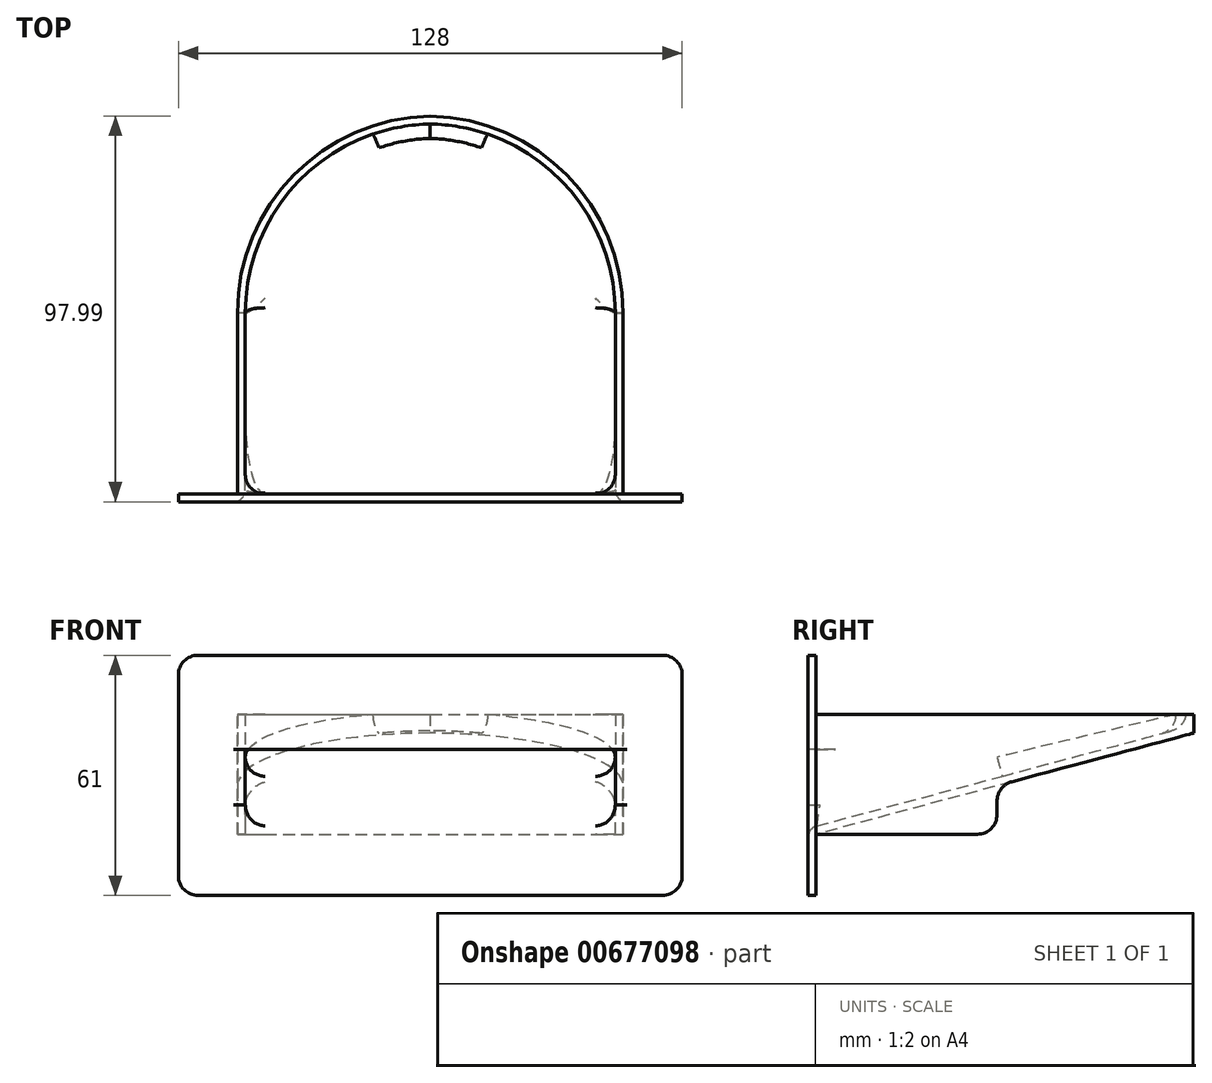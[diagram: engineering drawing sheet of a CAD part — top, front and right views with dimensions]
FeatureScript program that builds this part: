
annotation { "Feature Type Name" : "Feature", "Feature Type Description" : "" }
export const myFeature = defineFeature(function(context is Context, id is Id, definition is map)
    precondition{}
    {
        {
            var Q0;
            Q0=qCreatedBy(makeId("Front.planeOp"),FACE);
            var sketch = newSketch(context, id + "F0", { "sketchPlane" : qUnion([Q0])});
            skLineSegment(sketch, "E0.bottom", {"start": v(0, 0) * mm, "end": v(98, 0) * mm});
            skLineSegment(sketch, "E0.top", {"start": v(0, 31) * mm, "end": v(98, 31) * mm});
            skLineSegment(sketch, "E0.left", {"start": v(0, 0) * mm, "end": v(0, 31) * mm});
            skLineSegment(sketch, "E0.right", {"start": v(98, 0) * mm, "end": v(98, 31) * mm});
            skSolve(sketch);
        }
        {
            var Q0;
            Q0=makeQuery(id+"F0.imprint","IMPRINT",FACE,{"disambiguationData":[TD([[makeQuery(id+"F0.imprint","IMPRINT",EDGE,{"derivedFrom":sQuery(id+"F0.wireOp",EDGE,"E0.bottom")}),1.0]])]});
            extrude(context, id + "F1", {"entities" : qUnion([Q0]), "oppositeDirection" : true, "depth" : 98 * mm, "offsetDistance" : 25 * mm});
        }
        {
            var Q0;
            Q0=makeQuery(id+"F1.opExtrude","CAP_EDGE",EDGE,{"disambiguationData":[OSD([sQuery(id+"F0.wireOp",EDGE,"E0.right")])],"isStart":false});
            var Q1;
            Q1=makeQuery(id+"F1.opExtrude","CAP_EDGE",EDGE,{"disambiguationData":[OSD([sQuery(id+"F0.wireOp",EDGE,"E0.left")])],"isStart":false});
            fillet(context, id + "F2", {"entities" : qUnion([Q0, Q1]), "radius" : 50 * mm, "tangentPropagation" : true, "allowEdgeOverflow" : false});
        }
        {
            var Q0;
            Q0=qCreatedBy(makeId("Right.planeOp"),FACE);
            var sketch = newSketch(context, id + "F3", { "sketchPlane" : qUnion([Q0])});
            skLineSegment(sketch, "E1", {"start": v(0, 0) * mm, "end": v(111.58, 29.9) * mm});
            skLineSegment(sketch, "E2", {"start": v(111.58, 29.9) * mm, "end": v(111.58, 0) * mm});
            skLineSegment(sketch, "E3", {"start": v(111.58, 0) * mm, "end": v(0, 0) * mm});
            skSolve(sketch);
        }
        {
            var Q0;
            Q0=makeQuery(id+"F3.imprint","IMPRINT",FACE,{"disambiguationData":[TD([[makeQuery(id+"F3.imprint","IMPRINT",EDGE,{"derivedFrom":sQuery(id+"F3.wireOp",EDGE,"E1")}),-1.0]])]});
            extrude(context, id + "F4", {"entities" : qUnion([Q0]), "operationType" : NewBodyOperationType.REMOVE, "depth" : 200 * mm, "offsetDistance" : 25 * mm});
        }
        {
            var Q0;
            Q0=makeQuery(id+"F1.opExtrude","SWEPT_FACE",FACE,{"disambiguationData":[OSD([sQuery(id+"F0.wireOp",EDGE,"E0.top")])]});
            var Q1;
            Q1=makeQuery(id+"F1.opExtrude","CAP_FACE",FACE,{"disambiguationData":[OSD([sQuery(id+"F0.wireOp",EDGE,"E0.bottom"),sQuery(id+"F0.wireOp",EDGE,"E0.top"),sQuery(id+"F0.wireOp",EDGE,"E0.left"),sQuery(id+"F0.wireOp",EDGE,"E0.right")])],"isStart":true});
            shell(context, id + "F5", {"entities" : qUnion([Q0, Q1]), "thickness" : 2 * mm});
        }
        {
            var Q0;
            Q0=qCreatedBy(makeId("Front.planeOp"),FACE);
            var sketch = newSketch(context, id + "F6", { "sketchPlane" : qUnion([Q0])});
            skLineSegment(sketch, "E4.bottom", {"start": v(-15, -15) * mm, "end": v(113, -15) * mm});
            skLineSegment(sketch, "E4.top", {"start": v(-15, 46) * mm, "end": v(113, 46) * mm});
            skLineSegment(sketch, "E4.left", {"start": v(-15, -15) * mm, "end": v(-15, 46) * mm});
            skLineSegment(sketch, "E4.right", {"start": v(113, -15) * mm, "end": v(113, 46) * mm});
            skLineSegment(sketch, "E5.0", {"start": v(2, 2.07) * mm, "end": v(2, 31) * mm, "construction": true});
            skLineSegment(sketch, "E6.0", {"start": v(2, 2.07) * mm, "end": v(96, 2.07) * mm, "construction": true});
            skLineSegment(sketch, "E7.0", {"start": v(96, 2.07) * mm, "end": v(96, 31) * mm, "construction": true});
            skLineSegment(sketch, "E8.bottom", {"start": v(2, 2.07) * mm, "end": v(96, 2.07) * mm});
            skLineSegment(sketch, "E8.top", {"start": v(2, 22.07) * mm, "end": v(96, 22.07) * mm});
            skLineSegment(sketch, "E8.left", {"start": v(2, 2.07) * mm, "end": v(2, 22.07) * mm});
            skLineSegment(sketch, "E8.right", {"start": v(96, 2.07) * mm, "end": v(96, 22.07) * mm});
            skSolve(sketch);
        }
        {
            var Q0;
            Q0 = qSketchRegion(id + "F6", true);
            extrude(context, id + "F7", {"entities" : qUnion([Q0]), "operationType" : NewBodyOperationType.ADD, "oppositeDirection" : true, "depth" : 2 * mm, "offsetDistance" : 25 * mm});
        }
        {
            var Q0;
            Q0=makeQuery(id+"F1.opExtrude","SWEPT_FACE",FACE,{"disambiguationData":[OSD([sQuery(id+"F0.wireOp",EDGE,"E0.right")])]});
            var sketch = newSketch(context, id + "F8", { "sketchPlane" : qUnion([Q0])});
            skLineSegment(sketch, "E9.bottom", {"start": v(2, 31) * mm, "end": v(48, 31) * mm});
            skLineSegment(sketch, "E9.top", {"start": v(2, 0.54) * mm, "end": v(48, 0.54) * mm});
            skLineSegment(sketch, "E9.left", {"start": v(2, 31) * mm, "end": v(2, 0.54) * mm});
            skLineSegment(sketch, "E9.right", {"start": v(48, 31) * mm, "end": v(48, 0.54) * mm});
            skSolve(sketch);
        }
        {
            var Q0;
            Q0 = qSketchRegion(id + "F8", true);
            extrude(context, id + "F9", {"entities" : qUnion([Q0]), "operationType" : NewBodyOperationType.ADD, "oppositeDirection" : true, "depth" : 2 * mm, "offsetDistance" : 25 * mm});
        }
        {
            var Q0;
            Q0=makeQuery(id+"F1.opExtrude","SWEPT_FACE",FACE,{"disambiguationData":[OSD([sQuery(id+"F0.wireOp",EDGE,"E0.left")])]});
            var sketch = newSketch(context, id + "F10", { "sketchPlane" : qUnion([Q0])});
            skLineSegment(sketch, "E10.bottom", {"start": v(-2, 31) * mm, "end": v(-48, 31) * mm});
            skLineSegment(sketch, "E10.top", {"start": v(-2, 0.54) * mm, "end": v(-48, 0.54) * mm});
            skLineSegment(sketch, "E10.left", {"start": v(-2, 31) * mm, "end": v(-2, 0.54) * mm});
            skLineSegment(sketch, "E10.right", {"start": v(-48, 31) * mm, "end": v(-48, 0.54) * mm});
            skSolve(sketch);
        }
        {
            var Q0;
            Q0 = qSketchRegion(id + "F10", true);
            extrude(context, id + "F11", {"entities" : qUnion([Q0]), "operationType" : NewBodyOperationType.ADD, "oppositeDirection" : true, "depth" : 2 * mm, "offsetDistance" : 25 * mm});
        }
        {
            var Q0;
            Q0=makeQuery(id+"F11.opExtrude","SWEPT_EDGE",EDGE,{"disambiguationData":[OSD([sQuery(id+"F10.wireOp",EDGE,"E10.top"),sQuery(id+"F10.wireOp",EDGE,"E10.right")])]});
            var Q1;
            Q1=makeQuery(id+"F11.boolean.opBoolean","INTERSECT",EDGE,{"derivedFrom":[makeQuery(id+"F4.boolean.opBoolean","COPY",FACE,{"derivedFrom":makeQuery(id+"F4.opExtrude","SWEPT_FACE",FACE,{"disambiguationData":[OSD([sQuery(id+"F3.wireOp",EDGE,"E1")])]})}),makeQuery(id+"F11.opExtrude","SWEPT_FACE",FACE,{"disambiguationData":[OSD([sQuery(id+"F10.wireOp",EDGE,"E10.right")])]})]});
            var Q2;
            Q2=makeQuery(id+"F9.opExtrude","SWEPT_EDGE",EDGE,{"disambiguationData":[OSD([sQuery(id+"F8.wireOp",EDGE,"E9.top"),sQuery(id+"F8.wireOp",EDGE,"E9.right")])]});
            var Q3;
            Q3=makeQuery(id+"F9.boolean.opBoolean","INTERSECT",EDGE,{"derivedFrom":[makeQuery(id+"F4.boolean.opBoolean","COPY",FACE,{"derivedFrom":makeQuery(id+"F4.opExtrude","SWEPT_FACE",FACE,{"disambiguationData":[OSD([sQuery(id+"F3.wireOp",EDGE,"E1")])]})}),makeQuery(id+"F9.opExtrude","SWEPT_FACE",FACE,{"disambiguationData":[OSD([sQuery(id+"F8.wireOp",EDGE,"E9.right")])]})]});
            var Q4;
            Q4=makeQuery(id+"F7.opExtrude","SWEPT_EDGE",EDGE,{"disambiguationData":[OSD([sQuery(id+"F6.wireOp",EDGE,"E4.top"),sQuery(id+"F6.wireOp",EDGE,"E4.right")])]});
            var Q5;
            Q5=makeQuery(id+"F7.opExtrude","SWEPT_EDGE",EDGE,{"disambiguationData":[OSD([sQuery(id+"F6.wireOp",EDGE,"E4.top"),sQuery(id+"F6.wireOp",EDGE,"E4.left")])]});
            var Q6;
            Q6=makeQuery(id+"F7.opExtrude","SWEPT_EDGE",EDGE,{"disambiguationData":[OSD([sQuery(id+"F6.wireOp",EDGE,"E4.bottom"),sQuery(id+"F6.wireOp",EDGE,"E4.left")])]});
            var Q7;
            Q7=makeQuery(id+"F7.opExtrude","SWEPT_EDGE",EDGE,{"disambiguationData":[OSD([sQuery(id+"F6.wireOp",EDGE,"E4.bottom"),sQuery(id+"F6.wireOp",EDGE,"E4.right")])]});
            fillet(context, id + "F12", {"entities" : qUnion([Q0, Q1, Q2, Q3, Q4, Q5, Q6, Q7]), "radius" : 5 * mm, "tangentPropagation" : true, "allowEdgeOverflow" : false});
        }
        {
            var Q0;
            Q0=makeQuery(id+"F5.opShell","OFFSET_EDGE",EDGE,{"disambiguationData":[OSD([sQuery(id+"F3.wireOp",EDGE,"E1")])]});
            var Q1;
            {var subQ0=sQuery(id+"F3.wireOp",EDGE,"E1");var subQ1=sQuery(id+"F0.wireOp",EDGE,"E0.right");Q1=makeQuery(id+"F5.opShell","OFFSET_EDGE",EDGE,{"disambiguationData":[OSD([subQ1,subQ0]),TDD([makeQuery(id+"F4.boolean.opBoolean","INTERSECT",EDGE,{"derivedFrom":[makeQuery(id+"F1.opExtrude","SWEPT_FACE",FACE,{"disambiguationData":[OSD([subQ1])]}),makeQuery(id+"F4.opExtrude","SWEPT_FACE",FACE,{"disambiguationData":[OSD([subQ0])]})]})])]});}
            var Q2;
            Q2=makeQuery(id+"F7.opExtrude","SWEPT_EDGE",EDGE,{"disambiguationData":[OSD([sQuery(id+"F6.wireOp",EDGE,"E8.top"),sQuery(id+"F6.wireOp",EDGE,"E8.left")])]});
            var Q3;
            Q3=makeQuery(id+"F7.opExtrude","SWEPT_EDGE",EDGE,{"disambiguationData":[OSD([sQuery(id+"F6.wireOp",EDGE,"E8.top"),sQuery(id+"F6.wireOp",EDGE,"E8.right")])]});
            fillet(context, id + "F13", {"entities" : qUnion([Q0, Q1, Q2, Q3]), "radius" : 5 * mm, "tangentPropagation" : true, "allowEdgeOverflow" : false});
        }
        {
            var Q0;
            Q0=makeQuery(id+"F9.boolean.opBoolean","INTERSECT",EDGE,{"derivedFrom":[makeQuery(id+"F4.boolean.opBoolean","COPY",FACE,{"derivedFrom":makeQuery(id+"F4.opExtrude","SWEPT_FACE",FACE,{"disambiguationData":[OSD([sQuery(id+"F3.wireOp",EDGE,"E1")])]})}),makeQuery(id+"F9.opExtrude","CAP_FACE",FACE,{"disambiguationData":[OSD([sQuery(id+"F8.wireOp",EDGE,"E9.bottom"),sQuery(id+"F8.wireOp",EDGE,"E9.top"),sQuery(id+"F8.wireOp",EDGE,"E9.left"),sQuery(id+"F8.wireOp",EDGE,"E9.right")])],"isStart":false})]});
            var Q1;
            Q1=makeQuery(id+"F11.boolean.opBoolean","INTERSECT",EDGE,{"derivedFrom":[makeQuery(id+"F4.boolean.opBoolean","COPY",FACE,{"derivedFrom":makeQuery(id+"F4.opExtrude","SWEPT_FACE",FACE,{"disambiguationData":[OSD([sQuery(id+"F3.wireOp",EDGE,"E1")])]})}),makeQuery(id+"F11.opExtrude","CAP_FACE",FACE,{"disambiguationData":[OSD([sQuery(id+"F10.wireOp",EDGE,"E10.bottom"),sQuery(id+"F10.wireOp",EDGE,"E10.top"),sQuery(id+"F10.wireOp",EDGE,"E10.left"),sQuery(id+"F10.wireOp",EDGE,"E10.right")])],"isStart":false})]});
            var Q2;
            {var subQ0=sQuery(id+"F0.wireOp",EDGE,"E0.left");Q2=makeQuery(id+"F7.boolean.opBoolean","INTERSECT",EDGE,{"derivedFrom":[makeQuery(id+"F5.opShell","OFFSET_FACE",FACE,{"disambiguationData":[OSD([subQ0]),TDD([makeQuery(id+"F1.opExtrude","SWEPT_FACE",FACE,{"disambiguationData":[OSD([subQ0])]})])]}),makeQuery(id+"F7.opExtrude","CAP_FACE",FACE,{"disambiguationData":[OSD([sQuery(id+"F6.wireOp",EDGE,"E4.bottom"),sQuery(id+"F6.wireOp",EDGE,"E4.top"),sQuery(id+"F6.wireOp",EDGE,"E4.left"),sQuery(id+"F6.wireOp",EDGE,"E4.right"),sQuery(id+"F6.wireOp",EDGE,"E8.bottom"),sQuery(id+"F6.wireOp",EDGE,"E8.top"),sQuery(id+"F6.wireOp",EDGE,"E8.left"),sQuery(id+"F6.wireOp",EDGE,"E8.right")])],"isStart":false})]});}
            var Q3;
            {var subQ0=sQuery(id+"F0.wireOp",EDGE,"E0.right");Q3=makeQuery(id+"F7.boolean.opBoolean","INTERSECT",EDGE,{"derivedFrom":[makeQuery(id+"F5.opShell","OFFSET_FACE",FACE,{"disambiguationData":[OSD([subQ0]),TDD([makeQuery(id+"F1.opExtrude","SWEPT_FACE",FACE,{"disambiguationData":[OSD([subQ0])]})])]}),makeQuery(id+"F7.opExtrude","CAP_FACE",FACE,{"disambiguationData":[OSD([sQuery(id+"F6.wireOp",EDGE,"E4.bottom"),sQuery(id+"F6.wireOp",EDGE,"E4.top"),sQuery(id+"F6.wireOp",EDGE,"E4.left"),sQuery(id+"F6.wireOp",EDGE,"E4.right"),sQuery(id+"F6.wireOp",EDGE,"E8.bottom"),sQuery(id+"F6.wireOp",EDGE,"E8.top"),sQuery(id+"F6.wireOp",EDGE,"E8.left"),sQuery(id+"F6.wireOp",EDGE,"E8.right")])],"isStart":false})]});}
            fillet(context, id + "F14", {"entities" : qUnion([Q0, Q1, Q2, Q3]), "radius" : 5 * mm, "tangentPropagation" : true, "allowEdgeOverflow" : false});
        }
        {
            var Q0;
            Q0=makeQuery(id+"F5.opShell","OFFSET_EDGE",EDGE,{"disambiguationData":[OSD([sQuery(id+"F0.wireOp",EDGE,"E0.bottom"),sQuery(id+"F3.wireOp",EDGE,"E1"),sQuery(id+"F3.wireOp",EDGE,"E3")])]});
            fillet(context, id + "F15", {"entities" : qUnion([Q0]), "radius" : 3 * mm, "tangentPropagation" : true, "allowEdgeOverflow" : false});
        }
    });
